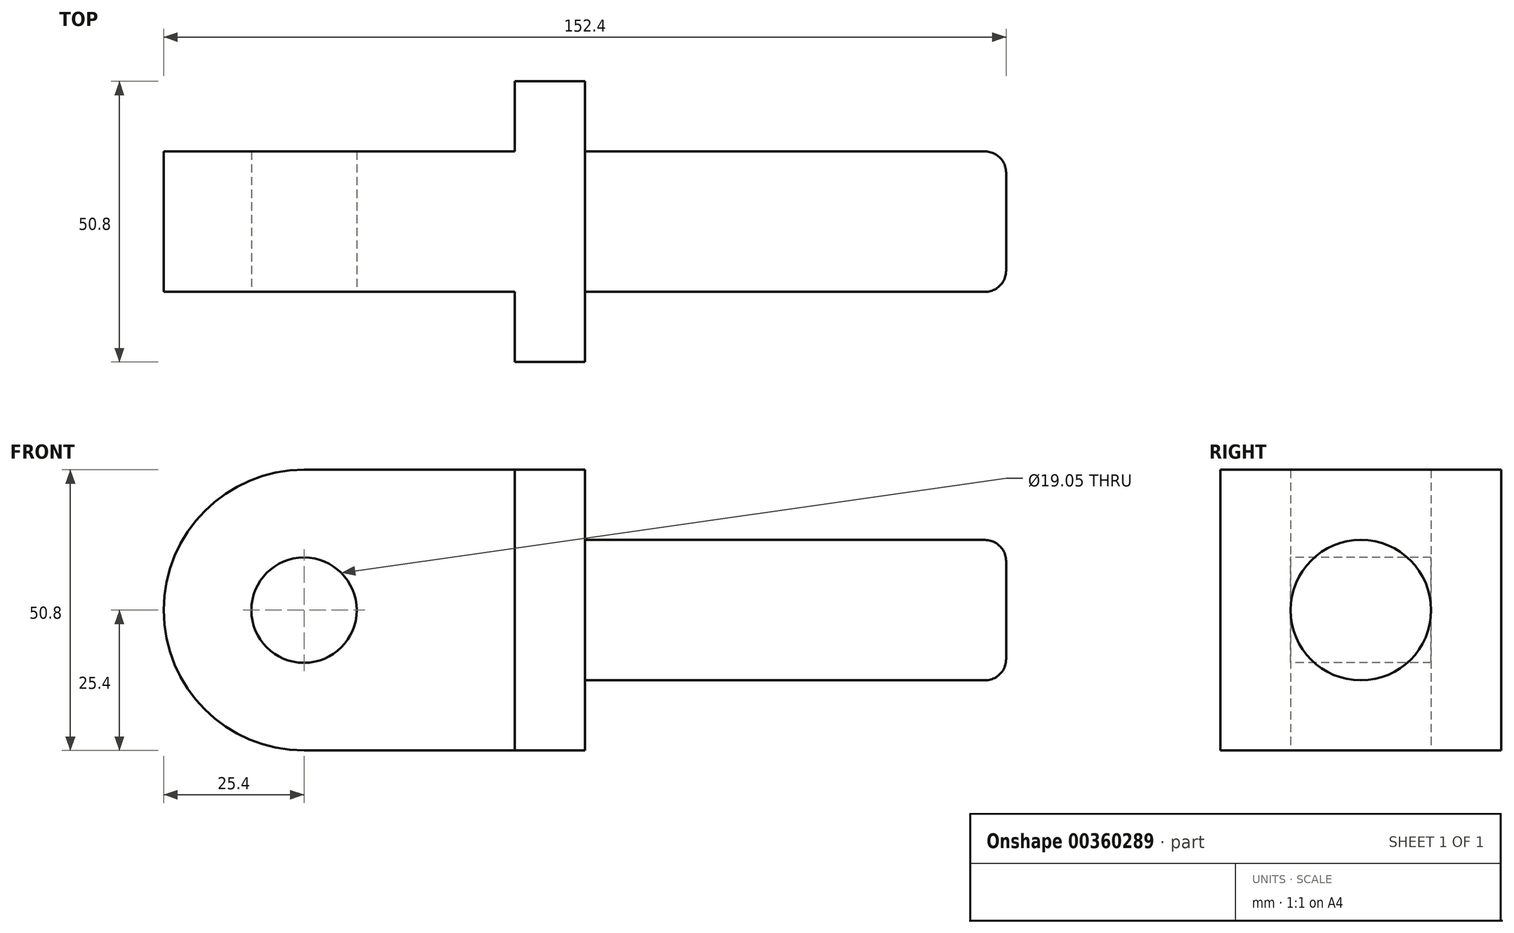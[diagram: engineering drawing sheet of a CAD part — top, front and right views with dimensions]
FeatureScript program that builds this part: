
annotation { "Feature Type Name" : "Feature", "Feature Type Description" : "" }
export const myFeature = defineFeature(function(context is Context, id is Id, definition is map)
    precondition{}
    {
        {
            var Q0;
            Q0=qCreatedBy(makeId("Front.planeOp"),FACE);
            var sketch = newSketch(context, id + "F0", { "sketchPlane" : qUnion([Q0])});
            skLineSegment(sketch, "E0", {"start": v(0, 0) * mm, "end": v(76.2, 0) * mm});
            skLineSegment(sketch, "E1", {"start": v(76.2, 0) * mm, "end": v(76.2, 50.8) * mm});
            skLineSegment(sketch, "E2", {"start": v(76.2, 50.8) * mm, "end": v(0, 50.8) * mm});
            skLineSegment(sketch, "E3", {"start": v(0, 50.8) * mm, "end": v(0, 0) * mm});
            skSolve(sketch);
        }
        {
            var Q0;
            Q0 = qSketchRegion(id + "F0", true);
            extrude(context, id + "F1", {"entities" : qUnion([Q0]), "depth" : 50.8 * mm});
        }
        {
            var Q0;
            Q0=makeQuery(id+"F1.opExtrude","SWEPT_FACE",FACE,{"disambiguationData":[OSD([sQuery(id+"F0.wireOp",EDGE,"E2")])]});
            var sketch = newSketch(context, id + "F2", { "sketchPlane" : qUnion([Q0])});
            skLineSegment(sketch, "E4", {"start": v(0, 0) * mm, "end": v(0, -12.7) * mm});
            skLineSegment(sketch, "E5", {"start": v(0, -12.7) * mm, "end": v(63.5, -12.7) * mm});
            skLineSegment(sketch, "E6", {"start": v(63.5, -12.7) * mm, "end": v(63.5, 0) * mm});
            skLineSegment(sketch, "E7", {"start": v(63.5, 0) * mm, "end": v(0, 0) * mm});
            skLineSegment(sketch, "E8", {"start": v(0, -50.8) * mm, "end": v(0, -38.1) * mm});
            skLineSegment(sketch, "E9", {"start": v(0, -38.1) * mm, "end": v(63.5, -38.1) * mm});
            skLineSegment(sketch, "E10", {"start": v(63.5, -38.1) * mm, "end": v(63.5, -50.8) * mm});
            skLineSegment(sketch, "E11", {"start": v(63.5, -50.8) * mm, "end": v(0, -50.8) * mm});
            skSolve(sketch);
        }
        {
            var Q0;
            Q0 = qSketchRegion(id + "F2", true);
            extrude(context, id + "F3", {"entities" : qUnion([Q0]), "operationType" : NewBodyOperationType.REMOVE, "oppositeDirection" : true, "depth" : 177.8 * mm});
        }
        {
            var Q0;
            Q0=makeQuery(id+"F3.boolean.opBoolean","COPY",FACE,{"derivedFrom":makeQuery(id+"F3.opExtrude","SWEPT_FACE",FACE,{"disambiguationData":[OSD([sQuery(id+"F2.wireOp",EDGE,"E9")])]})});
            var sketch = newSketch(context, id + "F4", { "sketchPlane" : qUnion([Q0])});
            skLineSegment(sketch, "E12", {"start": v(0, 50.8) * mm, "end": v(0, 25.4) * mm});
            skLineSegment(sketch, "E13", {"start": v(0, 25.4) * mm, "end": v(25.4, 25.4) * mm});
            skCircle(sketch, "E14", {"center": v(25.4, 25.4) * mm, "radius": 9.53 * mm});
            skSolve(sketch);
        }
        {
            var Q0;
            Q0 = qSketchRegion(id + "F4", true);
            extrude(context, id + "F5", {"entities" : qUnion([Q0]), "operationType" : NewBodyOperationType.REMOVE, "oppositeDirection" : true, "depth" : 127 * mm});
        }
        {
            var Q0;
            Q0=makeQuery(id+"F1.opExtrude","SWEPT_EDGE",EDGE,{"disambiguationData":[OSD([sQuery(id+"F0.wireOp",EDGE,"E0"),sQuery(id+"F0.wireOp",EDGE,"E3")])]});
            var Q1;
            Q1=makeQuery(id+"F1.opExtrude","SWEPT_EDGE",EDGE,{"disambiguationData":[OSD([sQuery(id+"F0.wireOp",EDGE,"E2"),sQuery(id+"F0.wireOp",EDGE,"E3")])]});
            fillet(context, id + "F6", {"entities" : qUnion([Q0, Q1]), "radius" : 25.4 * mm, "tangentPropagation" : true, "allowEdgeOverflow" : false});
        }
        {
            var Q0;
            Q0=makeQuery(id+"F1.opExtrude","SWEPT_FACE",FACE,{"disambiguationData":[OSD([sQuery(id+"F0.wireOp",EDGE,"E1")])]});
            var sketch = newSketch(context, id + "F7", { "sketchPlane" : qUnion([Q0])});
            skLineSegment(sketch, "E15", {"start": v(-25.4, 50.8) * mm, "end": v(-25.4, 0) * mm});
            skCircle(sketch, "E16", {"center": v(-25.4, 25.4) * mm, "radius": 12.7 * mm});
            skSolve(sketch);
        }
        {
            var Q0;
            Q0 = qSketchRegion(id + "F7", true);
            extrude(context, id + "F8", {"entities" : qUnion([Q0]), "operationType" : NewBodyOperationType.ADD, "depth" : 76.2 * mm});
        }
        {
            var Q0;
            Q0=makeQuery(id+"F8.opExtrude","CAP_EDGE",EDGE,{"disambiguationData":[OSD([sQuery(id+"F7.wireOp",EDGE,"E16")])],"isStart":false});
            var Q1;
            Q1=makeQuery(id+"F8.opExtrude","CAP_EDGE",EDGE,{"disambiguationData":[OSD([sQuery(id+"F7.wireOp",EDGE,"E16")])],"isStart":true});
            fillet(context, id + "F9", {"entities" : qUnion([Q0, Q1]), "radius" : 3.8 * mm, "tangentPropagation" : true, "allowEdgeOverflow" : false});
        }
    });
